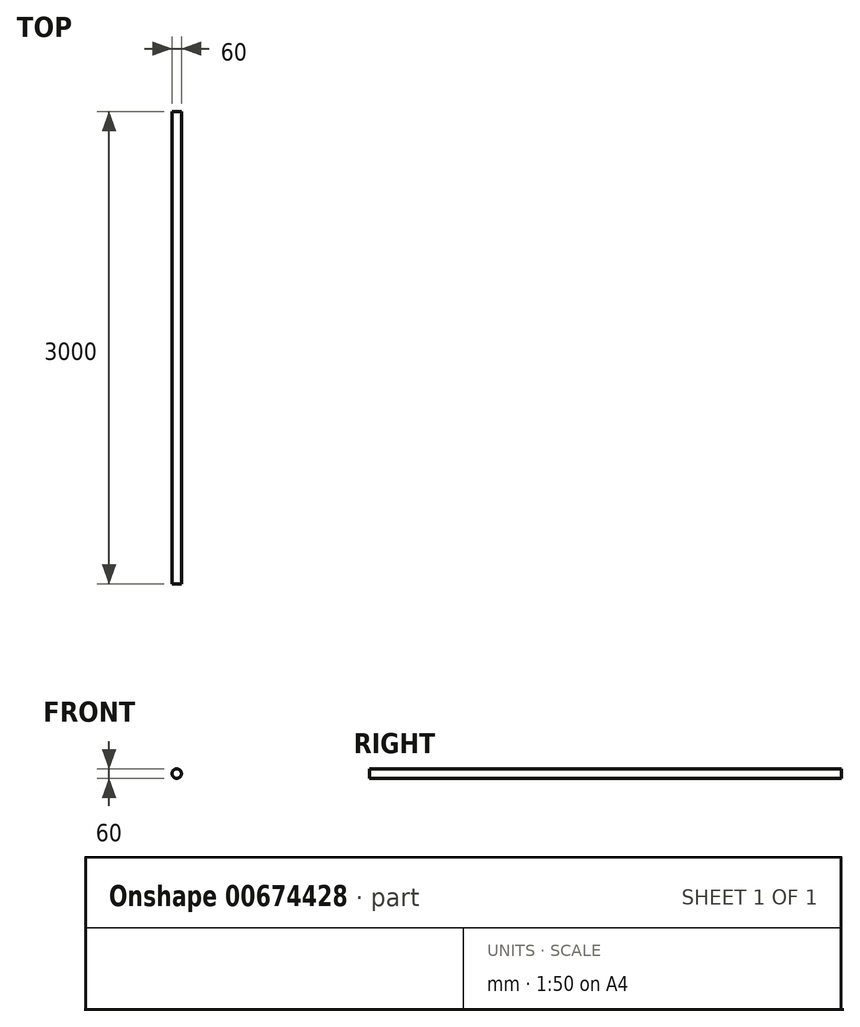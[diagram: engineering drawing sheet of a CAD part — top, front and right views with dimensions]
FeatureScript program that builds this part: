
annotation { "Feature Type Name" : "Feature", "Feature Type Description" : "" }
export const myFeature = defineFeature(function(context is Context, id is Id, definition is map)
    precondition{}
    {
        {
            var Q0;
            Q0=qCreatedBy(makeId("Front.planeOp"),FACE);
            var sketch = newSketch(context, id + "F0", { "sketchPlane" : qUnion([Q0])});
            skCircle(sketch, "E0", {"center": v(0, 0) * mm, "radius": 30 * mm});
            skSolve(sketch);
        }
        {
            var Q0;
            Q0 = qSketchRegion(id + "F0", true);
            extrude(context, id + "F1", {"entities" : qUnion([Q0]), "depth" : 3000 * mm, "offsetDistance" : 25 * mm});
        }
    });
